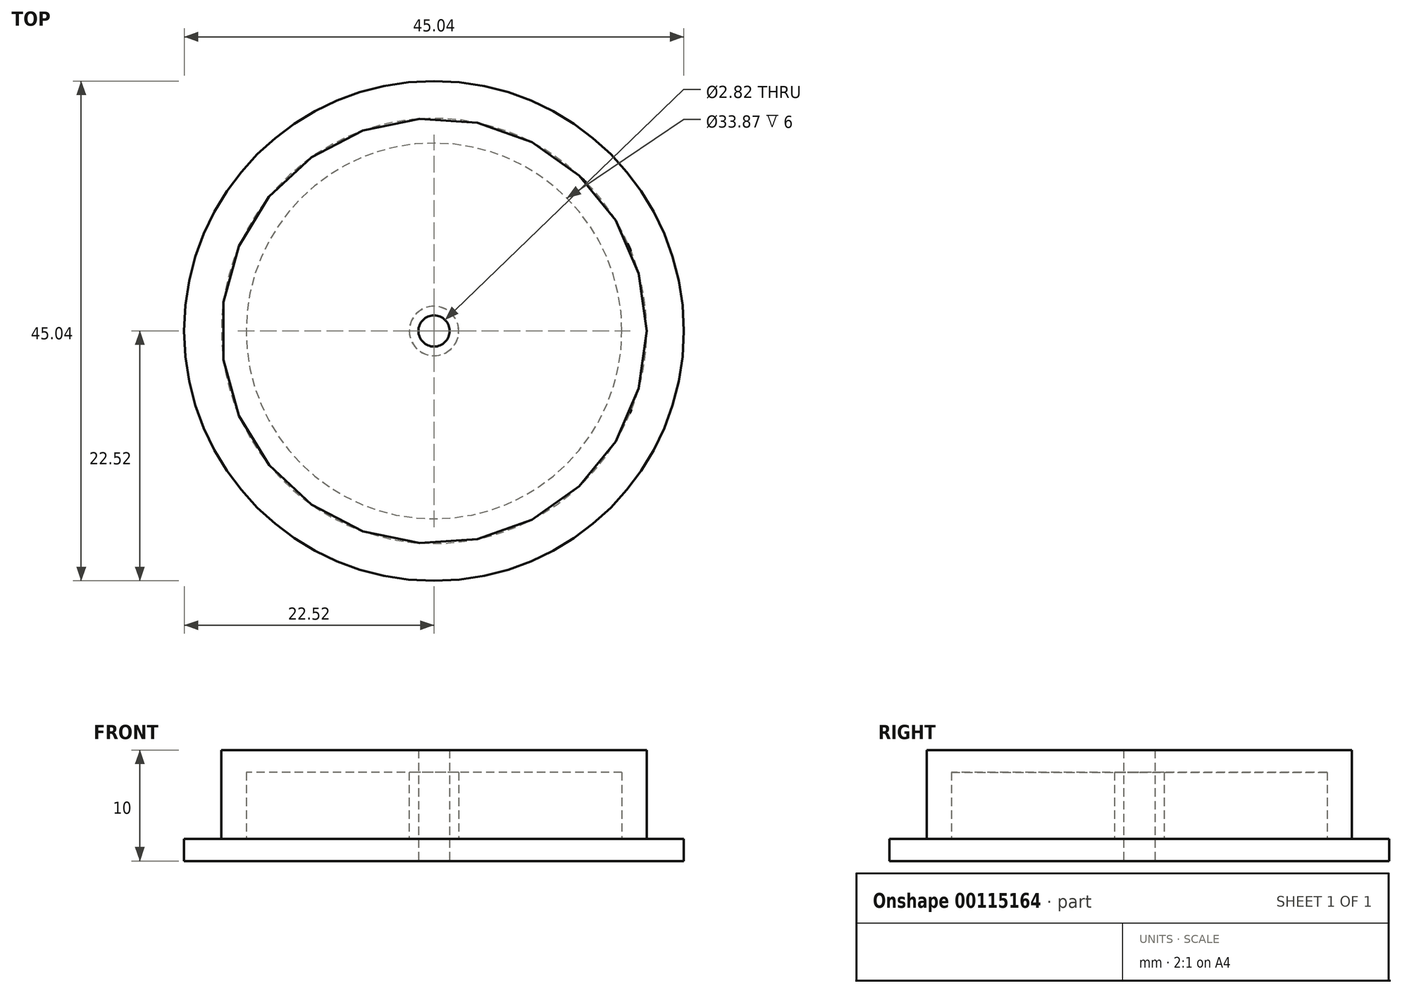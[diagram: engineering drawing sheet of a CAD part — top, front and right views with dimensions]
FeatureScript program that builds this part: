
annotation { "Feature Type Name" : "Feature", "Feature Type Description" : "" }
export const myFeature = defineFeature(function(context is Context, id is Id, definition is map)
    precondition{}
    {
        {
            var Q0;
            Q0=qCreatedBy(makeId("Top.planeOp"),FACE);
            var sketch = newSketch(context, id + "F0", { "sketchPlane" : qUnion([Q0])});
            skCircle(sketch, "E0", {"center": v(0, 0) * mm, "radius": 19.16 * mm});
            skCircle(sketch, "E1", {"center": v(0, 0) * mm, "radius": 22.52 * mm});
            skCircle(sketch, "E2", {"center": v(0, 0) * mm, "radius": 16.93 * mm});
            skCircle(sketch, "E3", {"center": v(0, 0) * mm, "radius": 1.41 * mm});
            skCircle(sketch, "E4", {"center": v(0, 0) * mm, "radius": 2.24 * mm});
            skSolve(sketch);
        }
        {
            var Q0;
            Q0=makeQuery(id+"F0.imprint","IMPRINT",FACE,{"disambiguationData":[TD([[makeQuery(id+"F0.imprint","IMPRINT",EDGE,{"derivedFrom":sQuery(id+"F0.wireOp",EDGE,"E0")}),-1.0]])]});
            extrude(context, id + "F1", {"entities" : qUnion([Q0]), "depth" : 2 * mm});
        }
        {
            var Q0;
            Q0=makeQuery(id+"F0.imprint","IMPRINT",FACE,{"disambiguationData":[TD([[makeQuery(id+"F0.imprint","IMPRINT",EDGE,{"derivedFrom":sQuery(id+"F0.wireOp",EDGE,"E0")}),1.0]])]});
            extrude(context, id + "F2", {"entities" : qUnion([Q0]), "operationType" : NewBodyOperationType.ADD, "depth" : 10 * mm});
        }
        {
            var Q0;
            Q0=makeQuery(id+"F0.imprint","IMPRINT",FACE,{"disambiguationData":[TD([[makeQuery(id+"F0.imprint","IMPRINT",EDGE,{"derivedFrom":sQuery(id+"F0.wireOp",EDGE,"E2")}),1.0]])]});
            extrude(context, id + "F3", {"entities" : qUnion([Q0]), "operationType" : NewBodyOperationType.ADD, "depth" : 2 * mm});
        }
        {
            var Q0;
            Q0=makeQuery(id+"F2.opExtrude","CAP_FACE",FACE,{"disambiguationData":[OSD([sQuery(id+"F0.wireOp",EDGE,"E0"),sQuery(id+"F0.wireOp",EDGE,"E2")])],"isStart":false});
            var sketch = newSketch(context, id + "F4", { "sketchPlane" : qUnion([Q0])});
            skCircle(sketch, "E5", {"center": v(0, 0) * mm, "radius": 19.16 * mm});
            skCircle(sketch, "E6", {"center": v(0, 0) * mm, "radius": 2.23 * mm});
            skSolve(sketch);
        }
        {
            var Q0;
            Q0=makeQuery(id+"F4.imprint","IMPRINT",FACE,{"disambiguationData":[TD([[makeQuery(id+"F4.imprint","IMPRINT",EDGE,{"derivedFrom":makeQuery(id+"F2.opExtrude","CAP_EDGE",EDGE,{"disambiguationData":[OSD([sQuery(id+"F0.wireOp",EDGE,"E2")])],"isStart":false})}),1.0]])]});
            var Q1;
            Q1=makeQuery(id+"F4.imprint","IMPRINT",FACE,{"disambiguationData":[TD([[makeQuery(id+"F4.imprint","IMPRINT",EDGE,{"derivedFrom":sQuery(id+"F4.wireOp",EDGE,"E5")}),1.0]])]});
            extrude(context, id + "F5", {"entities" : qUnion([Q0, Q1]), "operationType" : NewBodyOperationType.ADD, "oppositeDirection" : true, "depth" : 2 * mm});
        }
        {
            var Q0;
            Q0=makeQuery(id+"F0.imprint","IMPRINT",FACE,{"disambiguationData":[TD([[makeQuery(id+"F0.imprint","IMPRINT",EDGE,{"derivedFrom":sQuery(id+"F0.wireOp",EDGE,"E3")}),-1.0]])]});
            extrude(context, id + "F6", {"entities" : qUnion([Q0]), "operationType" : NewBodyOperationType.ADD, "depth" : 10 * mm});
        }
    });
